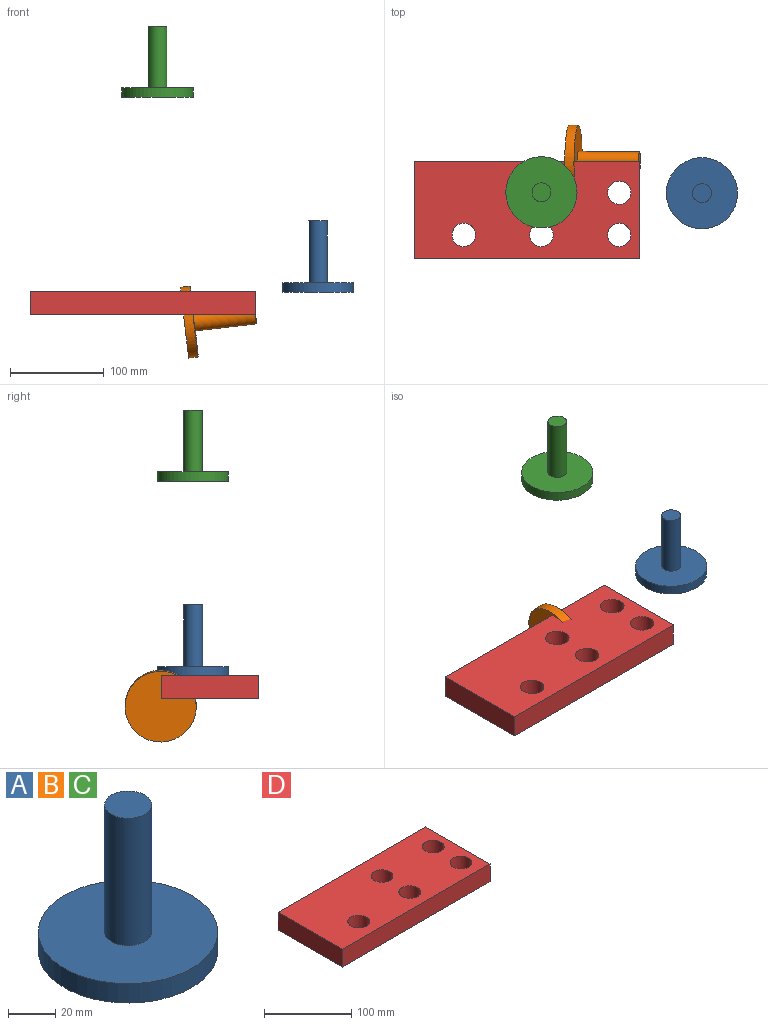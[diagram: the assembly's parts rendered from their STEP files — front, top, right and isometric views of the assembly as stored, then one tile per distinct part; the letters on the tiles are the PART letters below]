
ASSEMBLY  parts=4 mates=2
PART A: 5 faces, bbox 76x76x76 mm
  f0: cylinder r=37.98mm len=75.95mm, axis (0,0,-1), area 2386.1mm2, adj f1,f2
  f1: plane 75.95x75.95mm, normal (0,0,1), area 4215.3mm2, adj f0,f3
  f2: plane 75.95x75.95mm, normal (0,0,-1), area 4530.7mm2, adj f0
  f3: cylinder r=10.02mm len=66mm, axis (0,0,-1), area 4155.6mm2, adj f1,f4
  f4: plane 20.04x20.04mm, normal (0,0,1), area 315.5mm2, adj f3
PART B: same geometry as A
PART C: same geometry as A
PART D: 11 faces, bbox 240.2x104.2x25 mm
  f0: plane 240.15x25mm, normal (0,-1,0), area 6003.8mm2, adj f1,f3,f4,f5
  f1: plane 104.19x25mm, normal (1,0,0), area 2604.7mm2, adj f0,f2,f4,f5
  f2: plane 240.15x25mm, normal (0,1,0), area 6003.8mm2, adj f1,f3,f4,f5
  f3: plane 104.19x25mm, normal (-1,0,0), area 2604.7mm2, adj f0,f2,f4,f5
  f4: plane 240.15x104.19mm, normal (0,0,1), area 22566.7mm2, adj f0,f1,f2,f3,f6,f7,f8,f9
  f5: plane 240.15x104.19mm, normal (0,0,-1), area 22566.7mm2, adj f0,f1,f2,f3,f6,f7,f8,f9
  f6: cylinder r=12.5mm len=25mm, axis (0,0,1), area 1963.5mm2, adj f4,f5
  f7: cylinder r=12.5mm len=25mm, axis (0,0,1), area 1963.5mm2, adj f4,f5
  f8: cylinder r=12.5mm len=25mm, axis (0,0,1), area 1963.5mm2, adj f4,f5
  f9: cylinder r=12.5mm len=25mm, axis (0,0,1), area 1963.5mm2, adj f4,f5
  f10: cylinder r=12.5mm len=25mm, axis (0,0,1), area 1963.5mm2, adj f4,f5
PLACE A t=(-32.37,-45.97,-158.13)mm
PLACE B rot(axis=(0.05,1,0.04),83.5deg) t=(-174.5,-11.12,-190.86)mm
PLACE C t=(-203.62,-45.41,49.77)mm
PLACE D t=(-143,-95.67,-182.16)mm
MATE ball D.f5 <-> B.f3  axis (0,0,-1) through (-99,-11.88,-182.16)mm
MATE slider C.f3 <-> D.f9  axis (0,0,-1) through (-203.62,-45.41,92.77)mm
